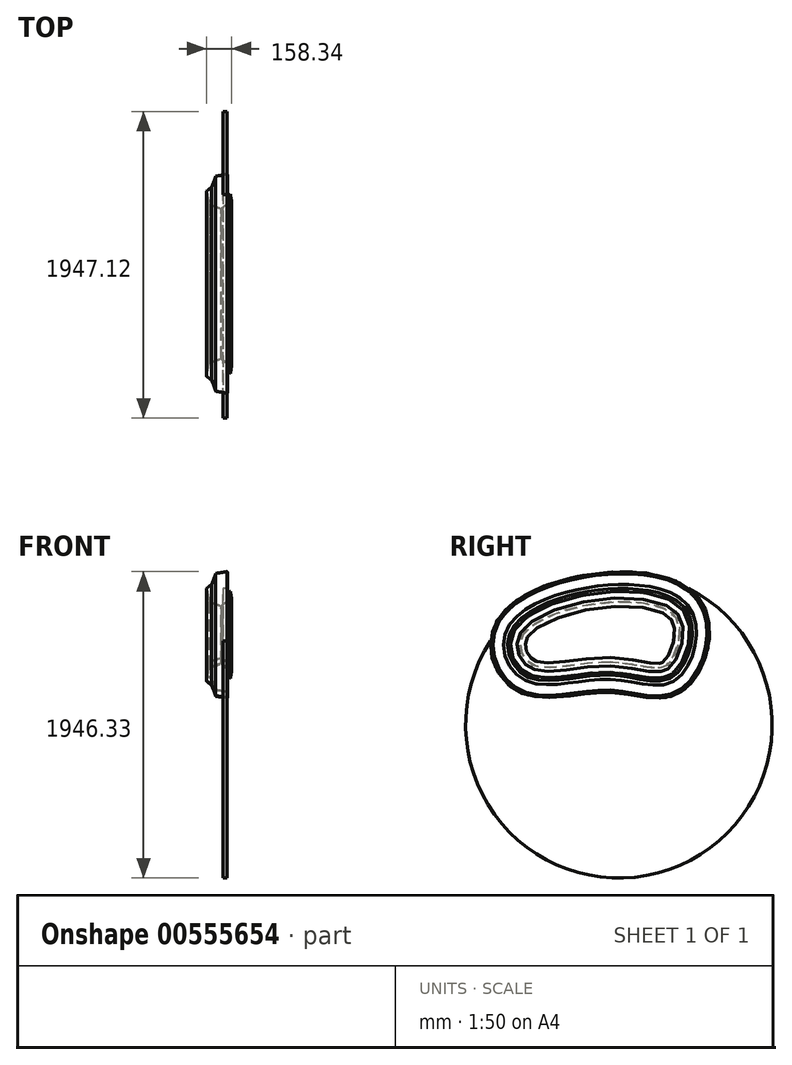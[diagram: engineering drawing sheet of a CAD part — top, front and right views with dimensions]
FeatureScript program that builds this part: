
annotation { "Feature Type Name" : "Feature", "Feature Type Description" : "" }
export const myFeature = defineFeature(function(context is Context, id is Id, definition is map)
    precondition{}
    {
        {
            var Q0;
            Q0=qCreatedBy(makeId("Front.planeOp"),FACE);
            var sketch = newSketch(context, id + "F0", { "sketchPlane" : qUnion([Q0])});
            skLineSegment(sketch, "E0.1", {"start": v(46.38, 56.8) * mm, "end": v(72.37, -11.77) * mm});
            skLineSegment(sketch, "E0.2", {"start": v(72.37, -11.77) * mm, "end": v(26, -68.56) * mm});
            skLineSegment(sketch, "E0.3", {"start": v(26, -68.56) * mm, "end": v(-46.38, -56.8) * mm});
            skLineSegment(sketch, "E0.4", {"start": v(-46.38, -56.8) * mm, "end": v(-72.37, 11.77) * mm});
            skPoint(sketch, "E0.0.midPoint", {"position": v(10.2, 62.68) * mm});
            skLineSegment(sketch, "E1.0", {"start": v(53.18, 98.58) * mm, "end": v(46.38, 56.8) * mm});
            skLineSegment(sketch, "E1.3", {"start": v(-105.16, 38.55) * mm, "end": v(-91.57, 122.12) * mm});
            skLineSegment(sketch, "E1.4", {"start": v(-91.57, 122.12) * mm, "end": v(-12.4, 152.13) * mm});
            skLineSegment(sketch, "E1.5", {"start": v(-12.4, 152.13) * mm, "end": v(53.18, 98.58) * mm});
            skPoint(sketch, "E1.0.midPoint", {"position": v(46.38, 56.8) * mm});
            skLineSegment(sketch, "E2.trimOffspring", {"start": v(-72.37, 11.77) * mm, "end": v(-105.16, 38.55) * mm});
            skPoint(sketch, "E1.1.start.orphan", {"position": v(39.58, 15) * mm});
            skPoint(sketch, "E1.cCircle.center.orphan", {"position": v(-26, 68.56) * mm});
            skSolve(sketch);
        }
        {
            var Q0;
            Q0=qCreatedBy(makeId("Right.planeOp"),FACE);
            var sketch = newSketch(context, id + "F1", { "sketchPlane" : qUnion([Q0])});
            skFitSpline(sketch, "E3", {"points": [v(0, 0) * mm, v(-556.7, 0) * mm, v(-633.62, 390.65) * mm, v(481.7, 516.02) * mm, v(424.56, 0) * mm, v(0, 0) * mm]});
            skSolve(sketch);
        }
        {
            var Q0;
            Q0=makeQuery(id+"F0.imprint","IMPRINT",FACE,{"disambiguationData":[TD([[makeQuery(id+"F0.imprint","IMPRINT",EDGE,{"derivedFrom":sQuery(id+"F0.wireOp",EDGE,"E0.1")}),-1.0]])]});
            var Q1;
            Q1=sQuery(id+"F1.wireOp",EDGE,"E3");
            sweep(context, id + "F2", {"profiles" : qUnion([Q0]), "path" : qUnion([Q1])});
        }
        {
            var Q0;
            Q0=makeQuery(id+"F2.opSweep","SWEPT_FACE",FACE,{"disambiguationData":[OSD([sQuery(id+"F0.wireOp",EDGE,"E0.2"),sQuery(id+"F1.wireOp",EDGE,"E3")])]});
            var Q1;
            Q1=makeQuery(id+"F2.opSweep","SWEPT_FACE",FACE,{"disambiguationData":[OSD([sQuery(id+"F0.wireOp",EDGE,"E0.1"),sQuery(id+"F1.wireOp",EDGE,"E3")])]});
            shell(context, id + "F3", {"entities" : qUnion([Q0, Q1]), "thickness" : 2.54 * mm});
        }
        {
            var Q0;
            Q0=qCreatedBy(makeId("Right.planeOp"),FACE);
            var sketch = newSketch(context, id + "F4", { "sketchPlane" : qUnion([Q0])});
            skFitSpline(sketch, "E4.0", {"points": [v(0, -68.56) * mm, v(-21.19, -67.74) * mm, v(-43.4, -68.2) * mm, v(-89.3, -71) * mm, v(-112.99, -73.33) * mm, v(-161.3, -78.98) * mm, v(-185.92, -82.3) * mm, v(-235.69, -88.95) * mm, v(-260.83, -92.3) * mm, v(-311.32, -97.94) * mm, v(-336.67, -100.25) * mm, v(-387.43, -102.66) * mm, v(-412.83, -102.77) * mm, v(-450.88, -100.17) * mm, v(-463.56, -98.84) * mm, v(-488.84, -95.05) * mm, v(-501.45, -92.57) * mm, v(-526.51, -86.25) * mm, v(-538.97, -82.4) * mm, v(-563.56, -73.07) * mm, v(-575.69, -67.6) * mm, v(-607.58, -50.47) * mm, v(-626.23, -37.46) * mm, v(-660.4, -7.89) * mm, v(-675.93, 8.68) * mm, v(-703.51, 44.66) * mm, v(-715.58, 64.09) * mm, v(-735.8, 105.21) * mm, v(-743.94, 126.92) * mm, v(-755.68, 172.04) * mm, v(-759.28, 195.46) * mm, v(-761.16, 243.27) * mm, v(-759.42, 267.66) * mm, v(-749.88, 316.38) * mm, v(-742.06, 340.7) * mm, v(-719.9, 387.93) * mm, v(-705.56, 410.85) * mm, v(-673.18, 450.6) * mm, v(-656.43, 467.47) * mm, v(-619.76, 499.05) * mm, v(-599.83, 513.78) * mm, v(-557.3, 541.44) * mm, v(-534.68, 554.35) * mm, v(-487.18, 578.52) * mm, v(-462.3, 589.77) * mm, v(-384.85, 621.11) * mm, v(-329.5, 638.8) * mm, v(-214.75, 667.57) * mm, v(-155.35, 678.64) * mm, v(-36, 693.63) * mm, v(23.93, 697.55) * mm, v(111.68, 697.46) * mm, v(140.57, 696.43) * mm, v(197.24, 692.26) * mm, v(225.01, 689.1) * mm, v(279.05, 680.5) * mm, v(305.32, 675.04) * mm, v(356, 661.57) * mm, v(380.4, 653.56) * mm, v(426.98, 634.56) * mm, v(449.14, 623.59) * mm, v(480.3, 604.47) * mm, v(490.33, 597.66) * mm, v(509.58, 583.07) * mm, v(518.8, 575.3) * mm, v(539.43, 555.73) * mm, v(550.22, 543.69) * mm, v(569.56, 518.43) * mm, v(578.12, 505.22) * mm, v(593.08, 478) * mm, v(599.48, 463.99) * mm, v(610.3, 435.46) * mm, v(614.7, 420.95) * mm, v(621.7, 391.67) * mm, v(624.29, 376.9) * mm, v(627.85, 347.28) * mm, v(628.81, 332.43) * mm, v(629.52, 287.98) * mm, v(627.07, 258.5) * mm, v(617.4, 200.84) * mm, v(610.17, 172.66) * mm, v(591.68, 118.56) * mm, v(580.42, 92.65) * mm, v(560.85, 56.2) * mm, v(553.88, 44.44) * mm, v(539.04, 21.88) * mm, v(531.17, 11.06) * mm, v(514.53, -9.5) * mm, v(505.76, -19.25) * mm, v(487.2, -37.51) * mm, v(477.43, -46.02) * mm, v(457.73, -60.8) * mm, v(448.07, -67.07) * mm, v(428.3, -78.1) * mm, v(418.2, -82.86) * mm, v(397.8, -90.92) * mm, v(387.48, -94.22) * mm, v(366.86, -99.52) * mm, v(356.54, -101.52) * mm, v(336.01, -104.44) * mm, v(325.8, -105.36) * mm, v(305.55, -106.32) * mm, v(295.5, -106.37) * mm, v(265.6, -105.53) * mm, v(246, -103.65) * mm, v(207.2, -98.58) * mm, v(188.01, -95.37) * mm, v(149.88, -88.65) * mm, v(130.94, -85.13) * mm, v(93.22, -78.63) * mm, v(74.45, -75.65) * mm, v(37.1, -70.97) * mm, v(18.5, -69.28) * mm, v(0, -68.56) * mm]});
            skCircle(sketch, "E5", {"center": v(54.26, -275.27) * mm, "radius": 973.56 * mm});
            skPoint(sketch, "E5.first.point", {"position": v(500.31, 590.1) * mm});
            skPoint(sketch, "E5.second.point", {"position": v(-759.25, 259.55) * mm});
            skPoint(sketch, "E5.third.point", {"position": v(-111.78, 684.03) * mm});
            skSolve(sketch);
        }
        {
            var Q0;
            {var subQ0=sQuery(id+"F4.wireOp",EDGE,"E5");var subQ1=sQuery(id+"F4.wireOp",EDGE,"E4.0");var subQ2=makeQuery(id+"F4.imprint","INTERSECT",VERTEX,{"disambiguationData":[OD(1.0)],"derivedFrom":[subQ1,subQ0]});Q0=makeQuery(id+"F4.imprint","IMPRINT",FACE,{"disambiguationData":[TD([[makeQuery(id+"F4.imprint","IMPRINT",EDGE,{"disambiguationData":[TD([[subQ2,1.0]])],"derivedFrom":subQ1}),1.0]])]});}
            extrude(context, id + "F5", {"entities" : qUnion([Q0]), "depth" : 25.4 * mm, "offsetDistance" : 25.4 * mm});
        }
        {
            var Q0;
            Q0=makeQuery(id+"F2.opSweep","SWEPT_BODY",BODY,{"disambiguationData":[OSD([sQuery(id+"F0.wireOp",EDGE,"E0.1"),sQuery(id+"F0.wireOp",EDGE,"E0.2"),sQuery(id+"F0.wireOp",EDGE,"E0.3"),sQuery(id+"F0.wireOp",EDGE,"E0.4"),sQuery(id+"F0.wireOp",EDGE,"E1.0"),sQuery(id+"F0.wireOp",EDGE,"E1.3"),sQuery(id+"F0.wireOp",EDGE,"E1.4"),sQuery(id+"F0.wireOp",EDGE,"E1.5"),sQuery(id+"F0.wireOp",EDGE,"E2.trimOffspring"),sQuery(id+"F1.wireOp",EDGE,"E3")])]});
            transform(context, id + "F6", {"entities" : qUnion([Q0]), "transformType" : TransformType.TRANSLATION_3D, "dx" : 0 * mm, "dy" : 0 * mm, "dz" : 0 * mm, "makeCopy" : true});
        }
        {
            var Q0;
            Q0=makeQuery(id+"F6.opPattern","COPY",BODY,{"derivedFrom":makeQuery(id+"F2.opSweep","SWEPT_BODY",BODY,{"disambiguationData":[OSD([sQuery(id+"F0.wireOp",EDGE,"E0.1"),sQuery(id+"F0.wireOp",EDGE,"E0.2"),sQuery(id+"F0.wireOp",EDGE,"E0.3"),sQuery(id+"F0.wireOp",EDGE,"E0.4"),sQuery(id+"F0.wireOp",EDGE,"E1.0"),sQuery(id+"F0.wireOp",EDGE,"E1.3"),sQuery(id+"F0.wireOp",EDGE,"E1.4"),sQuery(id+"F0.wireOp",EDGE,"E1.5"),sQuery(id+"F0.wireOp",EDGE,"E2.trimOffspring"),sQuery(id+"F1.wireOp",EDGE,"E3")])]}),"instanceName":"1"});
            deleteBodies(context, id + "F7", {"entities" : qUnion([Q0])});
        }
    });
